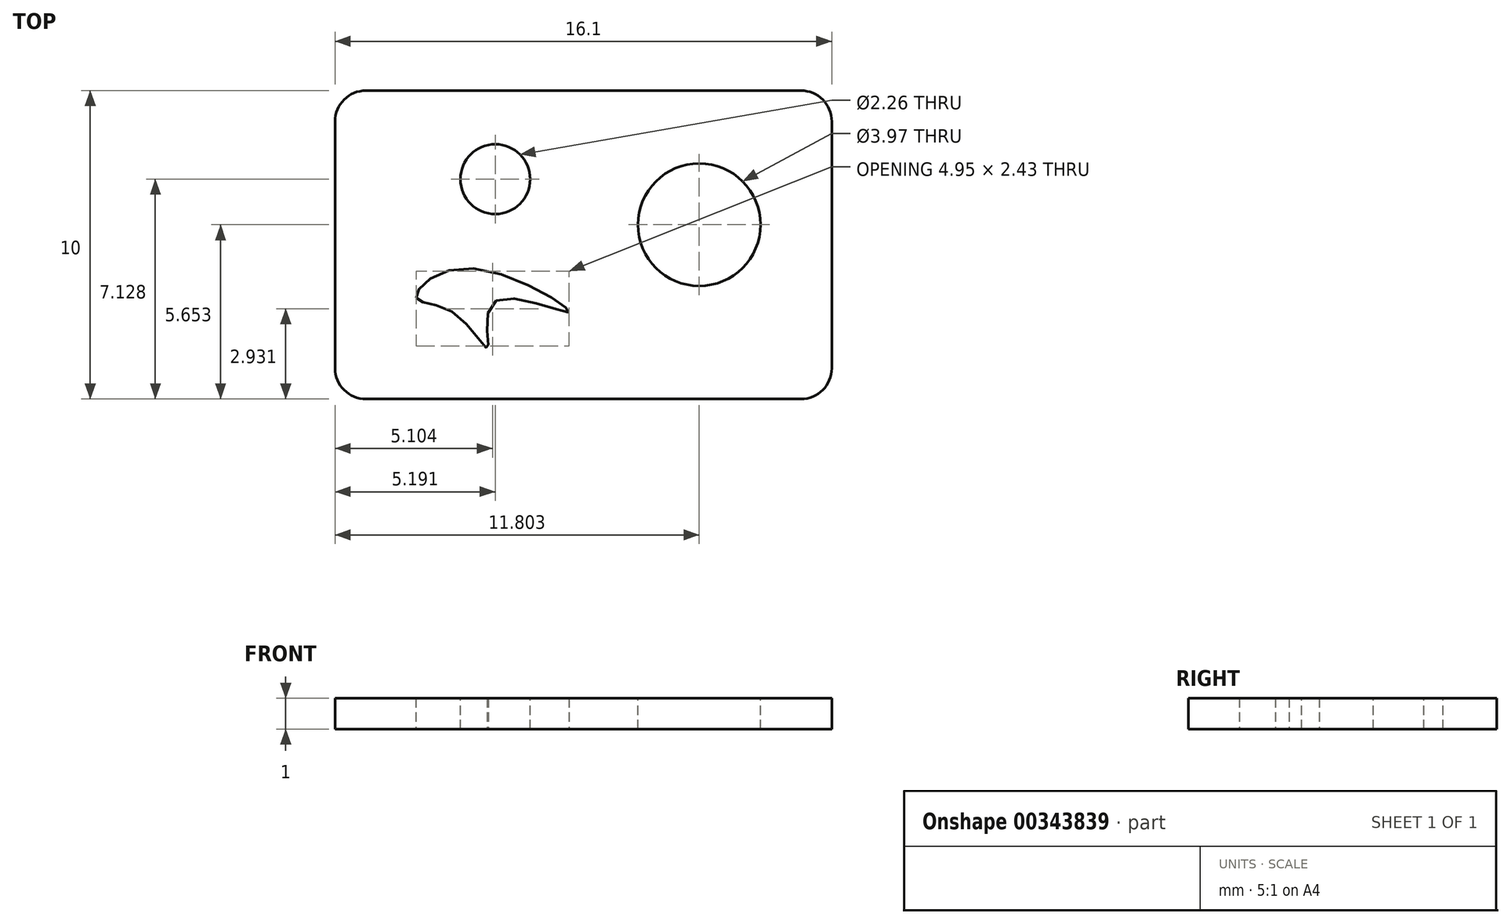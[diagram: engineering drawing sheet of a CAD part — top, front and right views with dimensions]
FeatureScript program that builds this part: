
annotation { "Feature Type Name" : "Feature", "Feature Type Description" : "" }
export const myFeature = defineFeature(function(context is Context, id is Id, definition is map)
    precondition{}
    {
        {
            var Q0;
            Q0=qCreatedBy(makeId("Top.planeOp"),FACE);
            var sketch = newSketch(context, id + "F0", { "sketchPlane" : qUnion([Q0])});
            skLineSegment(sketch, "E0.bottom", {"start": v(7.22, 5) * mm, "end": v(-8.88, 5) * mm});
            skLineSegment(sketch, "E0.top", {"start": v(7.22, -5) * mm, "end": v(-8.88, -5) * mm});
            skLineSegment(sketch, "E0.left", {"start": v(7.22, 5) * mm, "end": v(7.22, -5) * mm});
            skLineSegment(sketch, "E0.right", {"start": v(-8.88, 5) * mm, "end": v(-8.88, -5) * mm});
            skPoint(sketch, "E0.middle", {"position": v(-0.83, 0) * mm});
            skSolve(sketch);
        }
        {
            var Q0;
            Q0 = qSketchRegion(id + "F0", true);
            extrude(context, id + "F1", {"entities" : qUnion([Q0]), "depth" : 1 * mm});
        }
        {
            var Q0;
            Q0=makeQuery(id+"F1.opExtrude","CAP_FACE",FACE,{"disambiguationData":[OSD([sQuery(id+"F0.wireOp",EDGE,"E0.bottom"),sQuery(id+"F0.wireOp",EDGE,"E0.top"),sQuery(id+"F0.wireOp",EDGE,"E0.left"),sQuery(id+"F0.wireOp",EDGE,"E0.right")])],"isStart":false});
            var sketch = newSketch(context, id + "F2", { "sketchPlane" : qUnion([Q0])});
            skCircle(sketch, "E1", {"center": v(-3.69, 2.13) * mm, "radius": 1.13 * mm});
            skCircle(sketch, "E2", {"center": v(2.92, 0.65) * mm, "radius": 1.99 * mm});
            skFitSpline(sketch, "E3", {"points": [v(-6.25, -1.72) * mm, v(-4.61, -0.76) * mm, v(-1.31, -2.18) * mm, v(-3.72, -1.85) * mm, v(-3.93, -3.34) * mm, v(-5.07, -2.18) * mm, v(-6.25, -1.72) * mm]});
            skSolve(sketch);
        }
        {
            var Q0;
            Q0 = qSketchRegion(id + "F2", true);
            extrude(context, id + "F3", {"entities" : qUnion([Q0]), "operationType" : NewBodyOperationType.REMOVE, "oppositeDirection" : true, "depth" : 25 * mm});
        }
        {
            var Q0;
            Q0=makeQuery(id+"F1.opExtrude","SWEPT_EDGE",EDGE,{"disambiguationData":[OSD([sQuery(id+"F0.wireOp",EDGE,"E0.top"),sQuery(id+"F0.wireOp",EDGE,"E0.right")])]});
            var Q1;
            Q1=makeQuery(id+"F1.opExtrude","SWEPT_EDGE",EDGE,{"disambiguationData":[OSD([sQuery(id+"F0.wireOp",EDGE,"E0.bottom"),sQuery(id+"F0.wireOp",EDGE,"E0.right")])]});
            var Q2;
            Q2=makeQuery(id+"F1.opExtrude","SWEPT_EDGE",EDGE,{"disambiguationData":[OSD([sQuery(id+"F0.wireOp",EDGE,"E0.bottom"),sQuery(id+"F0.wireOp",EDGE,"E0.left")])]});
            var Q3;
            Q3=makeQuery(id+"F1.opExtrude","SWEPT_EDGE",EDGE,{"disambiguationData":[OSD([sQuery(id+"F0.wireOp",EDGE,"E0.top"),sQuery(id+"F0.wireOp",EDGE,"E0.left")])]});
            fillet(context, id + "F4", {"entities" : qUnion([Q0, Q1, Q2, Q3]), "radius" : 1 * mm, "tangentPropagation" : true, "allowEdgeOverflow" : false});
        }
    });
